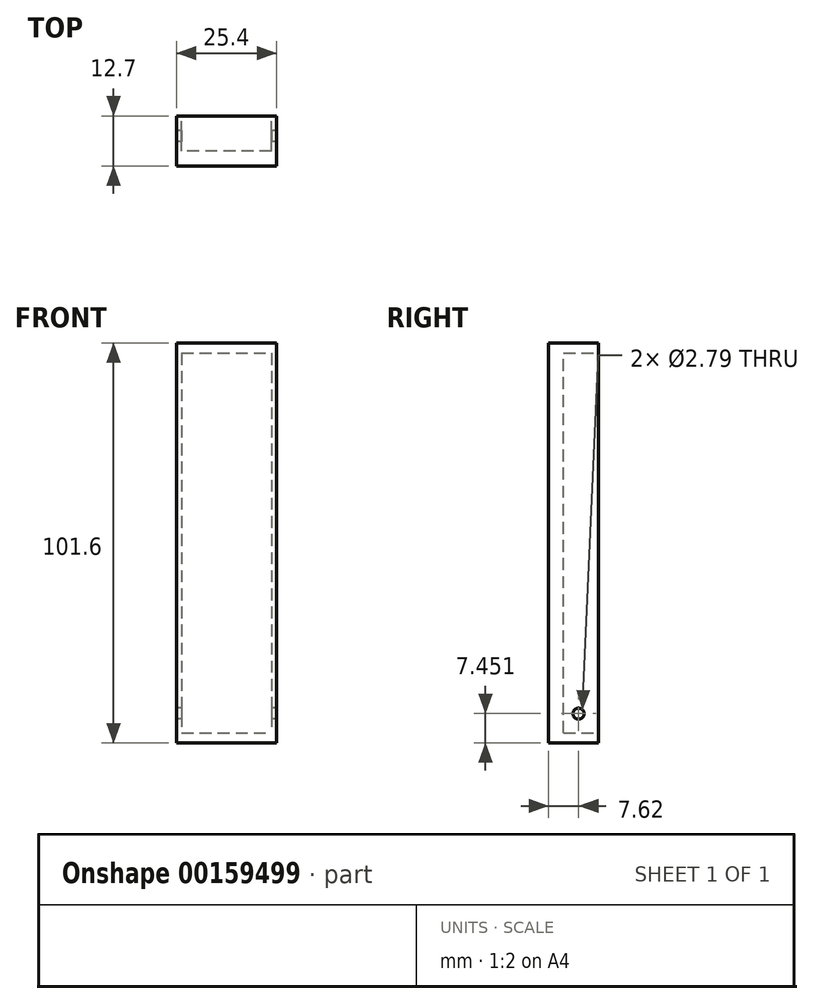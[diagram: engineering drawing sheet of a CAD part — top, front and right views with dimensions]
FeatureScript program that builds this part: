
annotation { "Feature Type Name" : "Feature", "Feature Type Description" : "" }
export const myFeature = defineFeature(function(context is Context, id is Id, definition is map)
    precondition{}
    {
        {
            var Q0;
            Q0=qCreatedBy(makeId("Front.planeOp"),FACE);
            var sketch = newSketch(context, id + "F0", { "sketchPlane" : qUnion([Q0])});
            skLineSegment(sketch, "E0.bottom", {"start": v(-12.7, -50.8) * mm, "end": v(12.7, -50.8) * mm});
            skLineSegment(sketch, "E0.top", {"start": v(-12.7, 50.8) * mm, "end": v(12.7, 50.8) * mm});
            skLineSegment(sketch, "E0.left", {"start": v(-12.7, -50.8) * mm, "end": v(-12.7, 50.8) * mm});
            skLineSegment(sketch, "E0.right", {"start": v(12.7, -50.8) * mm, "end": v(12.7, 50.8) * mm});
            skPoint(sketch, "E0.middle", {"position": v(0, 0) * mm});
            skSolve(sketch);
        }
        {
            var Q0;
            Q0 = qSketchRegion(id + "F0", true);
            extrude(context, id + "F1", {"entities" : qUnion([Q0]), "depth" : 7.62 * mm, "hasSecondDirection" : true, "secondDirectionOppositeDirection" : true, "secondDirectionDepth" : 5.08 * mm});
        }
        {
            var Q0;
            Q0=qCreatedBy(makeId("Front.planeOp"),FACE);
            var sketch = newSketch(context, id + "F2", { "sketchPlane" : qUnion([Q0])});
            skLineSegment(sketch, "E1.bottom", {"start": v(11.43, -48.26) * mm, "end": v(-11.43, -48.26) * mm});
            skLineSegment(sketch, "E1.top", {"start": v(11.43, 48.26) * mm, "end": v(-11.43, 48.26) * mm});
            skLineSegment(sketch, "E1.left", {"start": v(11.43, -48.26) * mm, "end": v(11.43, 48.26) * mm});
            skLineSegment(sketch, "E1.right", {"start": v(-11.43, -48.26) * mm, "end": v(-11.43, 48.26) * mm});
            skPoint(sketch, "E1.middle", {"position": v(0, 0) * mm});
            skSolve(sketch);
        }
        {
            var Q0;
            Q0 = qSketchRegion(id + "F2", true);
            extrude(context, id + "F3", {"entities" : qUnion([Q0]), "operationType" : NewBodyOperationType.REMOVE, "depth" : 3.8 * mm, "hasSecondDirection" : true, "secondDirectionOppositeDirection" : true, "secondDirectionDepth" : 25.4 * mm});
        }
        {
            var Q0;
            Q0=qCreatedBy(makeId("Right.planeOp"),FACE);
            var sketch = newSketch(context, id + "F4", { "sketchPlane" : qUnion([Q0])});
            skCircle(sketch, "E2", {"center": v(0, -43.35) * mm, "radius": 1.4 * mm});
            skPoint(sketch, "E2.first.point", {"position": v(-0.88, -44.43) * mm});
            skPoint(sketch, "E2.second.point", {"position": v(-0.77, -44.52) * mm});
            skPoint(sketch, "E2.third.point", {"position": v(-0.85, -44.46) * mm});
            skSolve(sketch);
        }
        {
            var Q0;
            Q0 = qSketchRegion(id + "F4", true);
            extrude(context, id + "F5", {"entities" : qUnion([Q0]), "operationType" : NewBodyOperationType.REMOVE, "depth" : 15.24 * mm, "hasSecondDirection" : true, "secondDirectionOppositeDirection" : true, "secondDirectionDepth" : 15.24 * mm});
        }
    });
